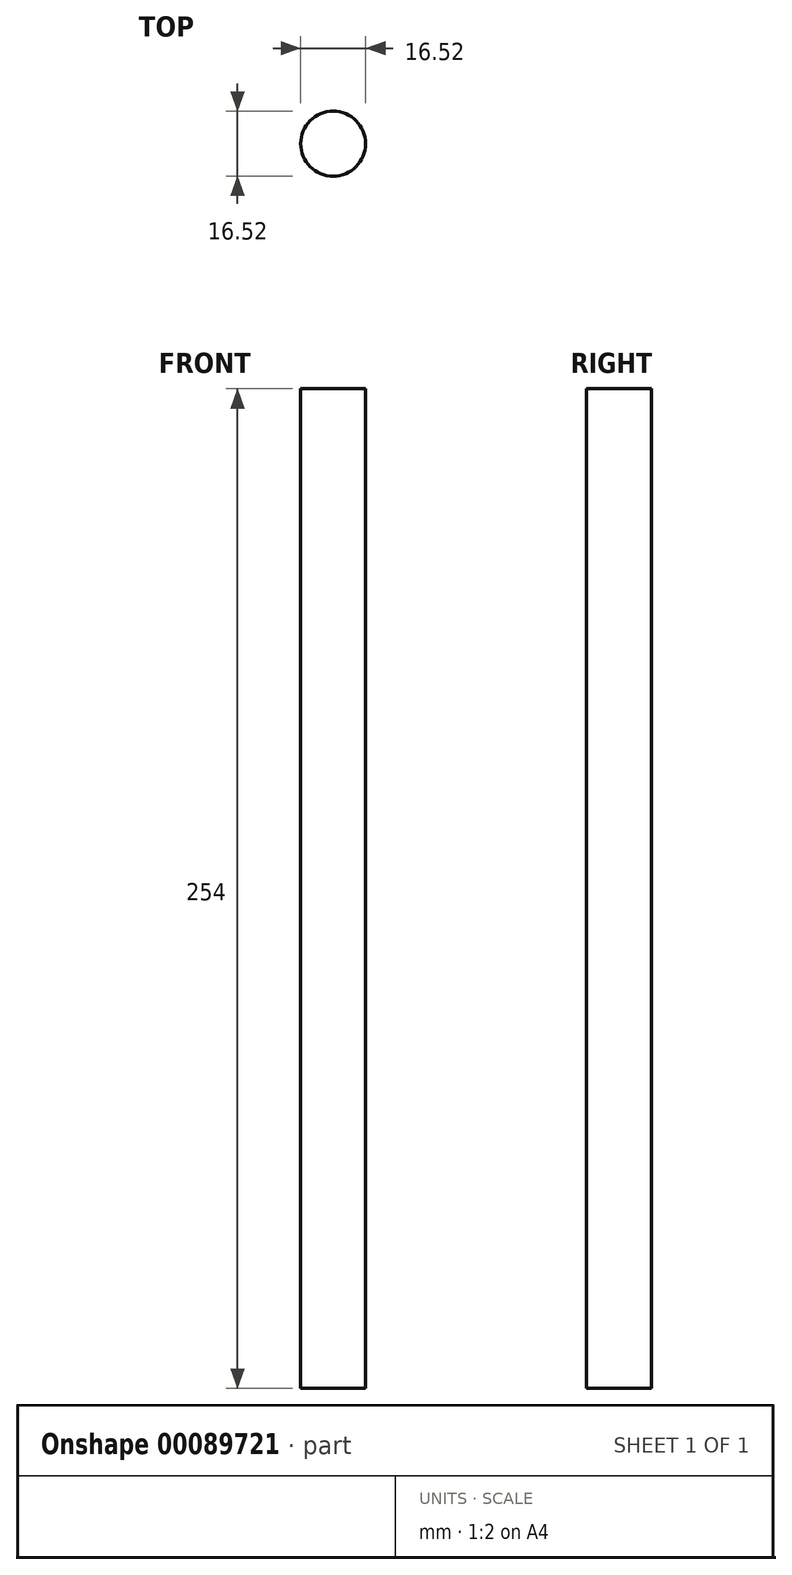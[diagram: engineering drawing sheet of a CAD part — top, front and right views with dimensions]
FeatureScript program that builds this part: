
annotation { "Feature Type Name" : "Feature", "Feature Type Description" : "" }
export const myFeature = defineFeature(function(context is Context, id is Id, definition is map)
    precondition{}
    {
        {
            var Q0;
            Q0=qCreatedBy(makeId("Top.planeOp"),FACE);
            var sketch = newSketch(context, id + "F0", { "sketchPlane" : qUnion([Q0])});
            skCircle(sketch, "E0", {"center": v(0, 0) * mm, "radius": 8.26 * mm});
            skSolve(sketch);
        }
        {
            var Q0;
            Q0=makeQuery(id+"F0.imprint","IMPRINT",FACE,{"disambiguationData":[TD([[makeQuery(id+"F0.imprint","IMPRINT",EDGE,{"derivedFrom":sQuery(id+"F0.wireOp",EDGE,"E0")}),1.0]])]});
            extrude(context, id + "F1", {"entities" : qUnion([Q0]), "depth" : 254 * mm});
        }
    });
